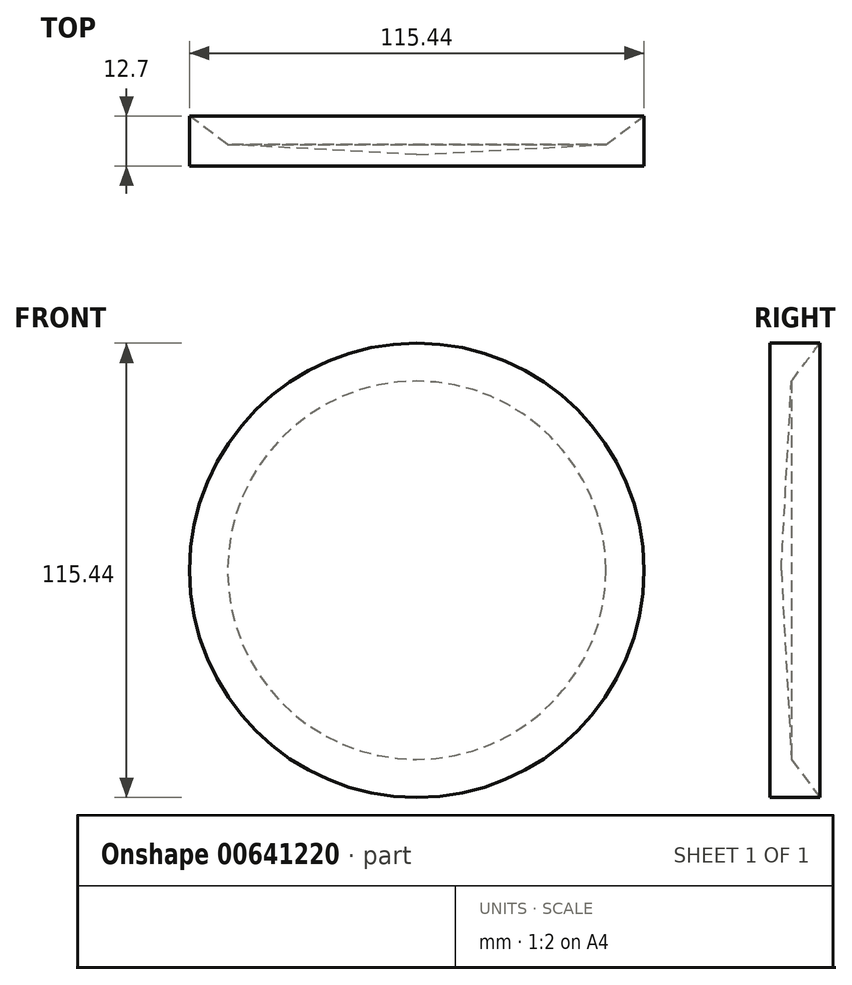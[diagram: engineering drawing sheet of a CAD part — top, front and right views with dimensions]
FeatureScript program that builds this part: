
annotation { "Feature Type Name" : "Feature", "Feature Type Description" : "" }
export const myFeature = defineFeature(function(context is Context, id is Id, definition is map)
    precondition{}
    {
        {
            var Q0;
            Q0=qCreatedBy(makeId("Front.planeOp"),FACE);
            var sketch = newSketch(context, id + "F0", { "sketchPlane" : qUnion([Q0])});
            skCircle(sketch, "E0", {"center": v(0, 0) * mm, "radius": 57.72 * mm});
            skSolve(sketch);
        }
        {
            var Q0;
            Q0 = qSketchRegion(id + "F0", true);
            extrude(context, id + "F1", {"entities" : qUnion([Q0]), "depth" : 12.7 * mm, "offsetDistance" : 25.4 * mm});
        }
        {
            var Q0;
            Q0=qCreatedBy(makeId("Top.planeOp"),FACE);
            var sketch = newSketch(context, id + "F2", { "sketchPlane" : qUnion([Q0])});
            skLineSegment(sketch, "E1.0", {"start": v(0, 0) * mm, "end": v(-57.72, 0) * mm});
            skLineSegment(sketch, "E2", {"start": v(-57.72, 0) * mm, "end": v(-48.05, -7.22) * mm});
            skLineSegment(sketch, "E3", {"start": v(-48.05, -7.22) * mm, "end": v(0, -9.82) * mm});
            skLineSegment(sketch, "E4", {"start": v(-57.72, 0) * mm, "end": v(0, 0) * mm});
            skLineSegment(sketch, "E5", {"start": v(0, -9.82) * mm, "end": v(0, 0) * mm});
            skPoint(sketch, "E6.orphan", {"position": v(57.72, 0) * mm});
            skSolve(sketch);
        }
        {
            var Q0;
            Q0 = qSketchRegion(id + "F2", true);
            var Q1;
            Q1=sQuery(id+"F2.wireOp",EDGE,"E5");
            revolve(context, id + "F3", {"operationType" : NewBodyOperationType.REMOVE, "entities" : qUnion([Q0]), "axis" : qUnion([Q1]), "revolveType" : RevolveType.FULL, "oppositeDirection" : true});
        }
    });
